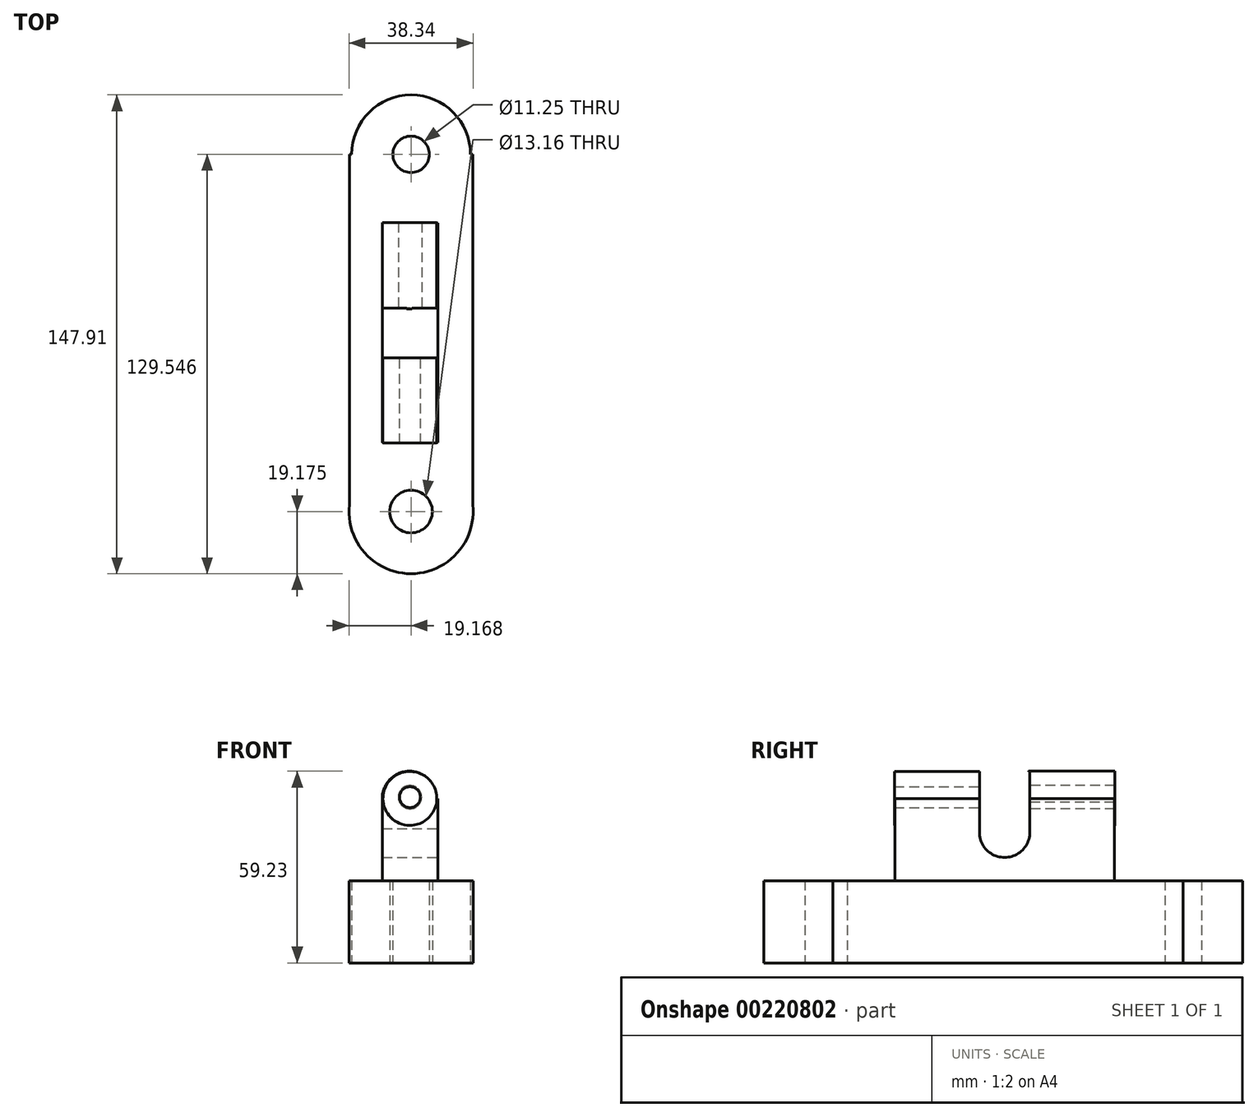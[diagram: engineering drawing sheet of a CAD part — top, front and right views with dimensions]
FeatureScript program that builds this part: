
annotation { "Feature Type Name" : "Feature", "Feature Type Description" : "" }
export const myFeature = defineFeature(function(context is Context, id is Id, definition is map)
    precondition{}
    {
        {
            var Q0;
            Q0=qCreatedBy(makeId("Top.planeOp"),FACE);
            var sketch = newSketch(context, id + "F0", { "sketchPlane" : qUnion([Q0])});
            skLineSegment(sketch, "E0.bottom", {"start": v(0, -55.19) * mm, "end": v(-38.12, -55.19) * mm});
            skLineSegment(sketch, "E0.top", {"start": v(0, 55.19) * mm, "end": v(-38.12, 55.19) * mm});
            skLineSegment(sketch, "E0.left", {"start": v(0, -55.19) * mm, "end": v(0, 55.19) * mm});
            skLineSegment(sketch, "E0.right", {"start": v(-38.12, -55.19) * mm, "end": v(-38.12, 55.19) * mm});
            skPoint(sketch, "E0.middle", {"position": v(-19.06, 0) * mm});
            skCircle(sketch, "E1", {"center": v(-19.06, 55.19) * mm, "radius": 18.36 * mm});
            skCircle(sketch, "E2", {"center": v(-19.06, -55.19) * mm, "radius": 19.17 * mm});
            skCircle(sketch, "E3", {"center": v(-19.06, -55.19) * mm, "radius": 6.58 * mm});
            skCircle(sketch, "E4", {"center": v(-19.06, 55.19) * mm, "radius": 5.63 * mm});
            skSolve(sketch);
        }
        {
            var Q0;
            {var subQ0=sQuery(id+"F0.wireOp",EDGE,"E1");var subQ1=sQuery(id+"F0.wireOp",EDGE,"E0.top");var subQ2=makeQuery(id+"F0.imprint","INTERSECT",VERTEX,{"disambiguationData":[OD(0.0)],"derivedFrom":[subQ1,subQ0]});Q0=makeQuery(id+"F0.imprint","IMPRINT",FACE,{"disambiguationData":[TD([[makeQuery(id+"F0.imprint","IMPRINT",EDGE,{"disambiguationData":[TD([[subQ2,-1.0]])],"derivedFrom":subQ1}),-1.0]])]});}
            var Q1;
            {var subQ0=sQuery(id+"F0.wireOp",EDGE,"E1");var subQ1=sQuery(id+"F0.wireOp",EDGE,"E0.top");var subQ2=makeQuery(id+"F0.imprint","INTERSECT",VERTEX,{"disambiguationData":[OD(0.0)],"derivedFrom":[subQ1,subQ0]});Q1=makeQuery(id+"F0.imprint","IMPRINT",FACE,{"disambiguationData":[TD([[makeQuery(id+"F0.imprint","IMPRINT",EDGE,{"disambiguationData":[TD([[subQ2,-1.0]])],"derivedFrom":subQ1}),1.0]])]});}
            var Q2;
            {var subQ1=sQuery(id+"F0.wireOp",EDGE,"E0.top");var subQ5=sQuery(id+"F0.wireOp",EDGE,"E0.left");var subQ6=makeQuery(id+"F0.imprint","INTERSECT",VERTEX,{"derivedFrom":[subQ1,subQ5]});Q2=makeQuery(id+"F0.imprint","IMPRINT",FACE,{"disambiguationData":[TD([[makeQuery(id+"F0.imprint","IMPRINT",EDGE,{"disambiguationData":[TD([[subQ6,-1.0]])],"derivedFrom":subQ1}),1.0]])]});}
            var Q3;
            {var subQ1=sQuery(id+"F0.wireOp",EDGE,"E0.bottom");var subQ5=sQuery(id+"F0.wireOp",EDGE,"E0.left");var subQ6=makeQuery(id+"F0.imprint","INTERSECT",VERTEX,{"derivedFrom":[subQ1,subQ5]});Q3=makeQuery(id+"F0.imprint","IMPRINT",FACE,{"disambiguationData":[TD([[makeQuery(id+"F0.imprint","IMPRINT",EDGE,{"disambiguationData":[TD([[subQ6,-1.0]])],"derivedFrom":subQ1}),-1.0]])]});}
            var Q4;
            {var subQ1=sQuery(id+"F0.wireOp",EDGE,"E0.bottom");var subQ5=sQuery(id+"F0.wireOp",EDGE,"E0.left");var subQ6=makeQuery(id+"F0.imprint","INTERSECT",VERTEX,{"derivedFrom":[subQ1,subQ5]});Q4=makeQuery(id+"F0.imprint","IMPRINT",FACE,{"disambiguationData":[TD([[makeQuery(id+"F0.imprint","IMPRINT",EDGE,{"disambiguationData":[TD([[subQ6,-1.0]])],"derivedFrom":subQ1}),1.0]])]});}
            extrude(context, id + "F1", {"entities" : qUnion([Q0, Q1, Q2, Q3, Q4]), "depth" : 25.4 * mm});
        }
        {
            var Q0;
            Q0=qCreatedBy(makeId("Top.planeOp"),FACE);
            var sketch = newSketch(context, id + "F2", { "sketchPlane" : qUnion([Q0])});
            skPoint(sketch, "E5.middle", {"position": v(-12.17, 22.62) * mm});
            skPoint(sketch, "E5.bottom.end.orphan", {"position": v(-9.57, 38.5) * mm});
            skPoint(sketch, "E5.bottom.start.orphan", {"position": v(-14.76, 38.5) * mm});
            skPoint(sketch, "E5.top.end.orphan", {"position": v(-9.57, 6.75) * mm});
            skPoint(sketch, "E5.top.start.orphan", {"position": v(-14.76, 6.75) * mm});
            skLineSegment(sketch, "E6.bottom", {"start": v(-27.9, 33.92) * mm, "end": v(-10.72, 33.92) * mm});
            skLineSegment(sketch, "E6.top", {"start": v(-27.9, -33.92) * mm, "end": v(-10.72, -33.92) * mm});
            skLineSegment(sketch, "E6.left", {"start": v(-27.9, 33.92) * mm, "end": v(-27.9, -33.92) * mm});
            skLineSegment(sketch, "E6.right", {"start": v(-10.72, 33.92) * mm, "end": v(-10.72, -33.92) * mm});
            skPoint(sketch, "E6.middle", {"position": v(-19.3, 0) * mm});
            skSolve(sketch);
        }
        {
            var Q0;
            Q0 = qSketchRegion(id + "F2", true);
            extrude(context, id + "F3", {"entities" : qUnion([Q0]), "operationType" : NewBodyOperationType.ADD, "depth" : 50.8 * mm});
        }
        {
            var Q0;
            Q0=qCreatedBy(makeId("Front.planeOp"),FACE);
            var sketch = newSketch(context, id + "F4", { "sketchPlane" : qUnion([Q0])});
            skCircle(sketch, "E7", {"center": v(-19.42, 50.8) * mm, "radius": 8.32 * mm});
            skSolve(sketch);
        }
        {
            var Q0;
            Q0 = qSketchRegion(id + "F4", true);
            extrude(context, id + "F5", {"entities" : qUnion([Q0]), "operationType" : NewBodyOperationType.ADD, "depth" : 34.04 * mm});
        }
        {
            var Q0;
            Q0=qCreatedBy(makeId("Front.planeOp"),FACE);
            var sketch = newSketch(context, id + "F6", { "sketchPlane" : qUnion([Q0])});
            skCircle(sketch, "E8", {"center": v(-19.55, 50.8) * mm, "radius": 8.42 * mm});
            skSolve(sketch);
        }
        {
            var Q0;
            Q0 = qSketchRegion(id + "F6", true);
            extrude(context, id + "F7", {"entities" : qUnion([Q0]), "operationType" : NewBodyOperationType.ADD, "oppositeDirection" : true, "depth" : 34.04 * mm});
        }
        {
            var Q0;
            Q0=qCreatedBy(makeId("Right.planeOp"),FACE);
            var sketch = newSketch(context, id + "F8", { "sketchPlane" : qUnion([Q0])});
            skCircle(sketch, "E9", {"center": v(0, 40.36) * mm, "radius": 7.8 * mm});
            skSolve(sketch);
        }
        {
            var Q0;
            Q0 = qSketchRegion(id + "F8", true);
            extrude(context, id + "F9", {"entities" : qUnion([Q0]), "operationType" : NewBodyOperationType.REMOVE, "endBound" : BoundingType.THROUGH_ALL, "oppositeDirection" : true, "depth" : 25.4 * mm});
        }
        {
            var Q0;
            Q0=qCreatedBy(makeId("Right.planeOp"),FACE);
            var sketch = newSketch(context, id + "F10", { "sketchPlane" : qUnion([Q0])});
            skLineSegment(sketch, "E10.bottom", {"start": v(-7.7, 40.65) * mm, "end": v(7.7, 40.65) * mm});
            skLineSegment(sketch, "E10.top", {"start": v(-7.7, 59.19) * mm, "end": v(7.7, 59.19) * mm});
            skLineSegment(sketch, "E10.left", {"start": v(-7.7, 40.65) * mm, "end": v(-7.7, 59.19) * mm});
            skLineSegment(sketch, "E10.right", {"start": v(7.7, 40.65) * mm, "end": v(7.7, 59.19) * mm});
            skSolve(sketch);
        }
        {
            var Q0;
            Q0 = qSketchRegion(id + "F10", true);
            extrude(context, id + "F11", {"entities" : qUnion([Q0]), "operationType" : NewBodyOperationType.REMOVE, "endBound" : BoundingType.THROUGH_ALL, "oppositeDirection" : true, "depth" : 25.4 * mm});
        }
        {
            var Q0;
            Q0=qCreatedBy(makeId("Right.planeOp"),FACE);
            var sketch = newSketch(context, id + "F12", { "sketchPlane" : qUnion([Q0])});
            skLineSegment(sketch, "E11.bottom", {"start": v(0, 55.48) * mm, "end": v(7.42, 55.48) * mm});
            skLineSegment(sketch, "E11.top", {"start": v(0, 64.6) * mm, "end": v(7.42, 64.6) * mm});
            skLineSegment(sketch, "E11.left", {"start": v(0, 55.48) * mm, "end": v(0, 64.6) * mm});
            skLineSegment(sketch, "E11.right", {"start": v(7.42, 55.48) * mm, "end": v(7.42, 64.6) * mm});
            skSolve(sketch);
        }
        {
            var Q0;
            Q0 = qSketchRegion(id + "F12", true);
            extrude(context, id + "F13", {"entities" : qUnion([Q0]), "operationType" : NewBodyOperationType.REMOVE, "endBound" : BoundingType.THROUGH_ALL, "oppositeDirection" : true, "depth" : 25.4 * mm});
        }
        {
            var Q0;
            Q0=qCreatedBy(makeId("Front.planeOp"),FACE);
            var sketch = newSketch(context, id + "F14", { "sketchPlane" : qUnion([Q0])});
            skCircle(sketch, "E12", {"center": v(-19.4, 51.2) * mm, "radius": 3.6 * mm});
            skSolve(sketch);
        }
        {
            var Q0;
            Q0 = qSketchRegion(id + "F14", true);
            extrude(context, id + "F15", {"entities" : qUnion([Q0]), "operationType" : NewBodyOperationType.REMOVE, "endBound" : BoundingType.THROUGH_ALL, "oppositeDirection" : true, "depth" : 25.4 * mm});
        }
        {
            var Q0;
            Q0 = qSketchRegion(id + "F14", true);
            extrude(context, id + "F16", {"entities" : qUnion([Q0]), "operationType" : NewBodyOperationType.REMOVE, "endBound" : BoundingType.THROUGH_ALL, "oppositeDirection" : true, "depth" : 25.4 * mm});
        }
        {
            var Q0;
            Q0=qCreatedBy(makeId("Front.planeOp"),FACE);
            var sketch = newSketch(context, id + "F17", { "sketchPlane" : qUnion([Q0])});
            skCircle(sketch, "E13", {"center": v(-19.4, 51.2) * mm, "radius": 3.23 * mm});
            skSolve(sketch);
        }
        {
            var Q0;
            Q0 = qSketchRegion(id + "F17", true);
            extrude(context, id + "F18", {"entities" : qUnion([Q0]), "operationType" : NewBodyOperationType.REMOVE, "depth" : 36.07 * mm});
        }
    });
